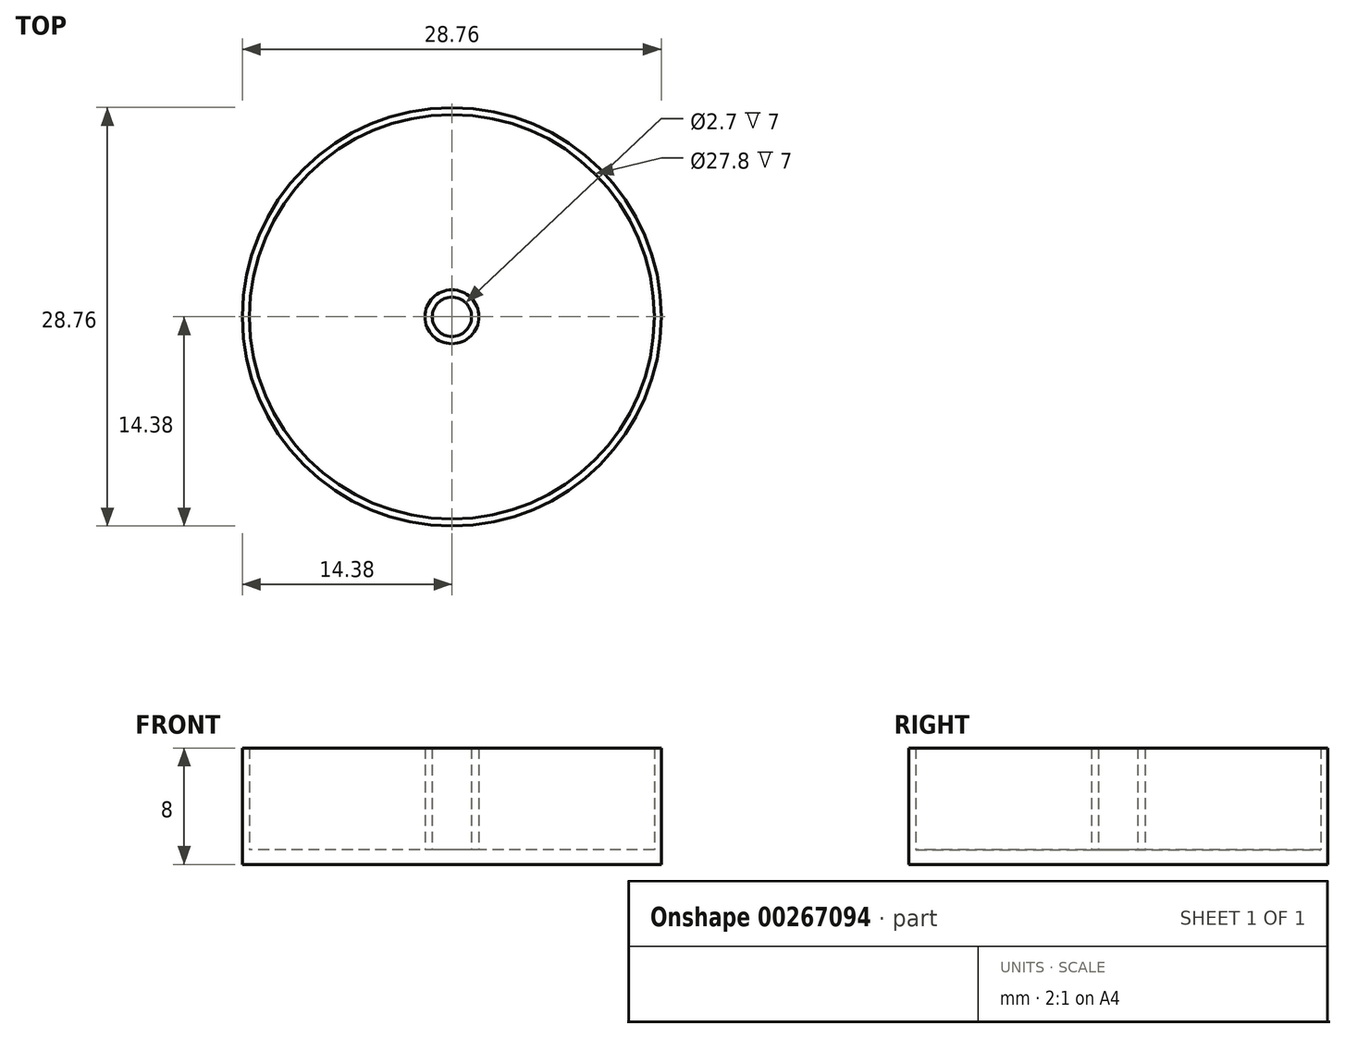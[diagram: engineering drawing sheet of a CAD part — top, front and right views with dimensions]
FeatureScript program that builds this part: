
annotation { "Feature Type Name" : "Feature", "Feature Type Description" : "" }
export const myFeature = defineFeature(function(context is Context, id is Id, definition is map)
    precondition{}
    {
        {
            var Q0;
            Q0=qCreatedBy(makeId("Top.planeOp"),FACE);
            var sketch = newSketch(context, id + "F0", { "sketchPlane" : qUnion([Q0])});
            skCircle(sketch, "E0", {"center": v(0, 0) * mm, "radius": 14.38 * mm});
            skCircle(sketch, "E1", {"center": v(0, 0) * mm, "radius": 13.9 * mm});
            skCircle(sketch, "E2", {"center": v(0, 0) * mm, "radius": 1.35 * mm});
            skCircle(sketch, "E3", {"center": v(0, 0) * mm, "radius": 1.85 * mm});
            skSolve(sketch);
        }
        {
            var Q0;
            Q0=makeQuery(id+"F0.imprint","IMPRINT",FACE,{"disambiguationData":[TD([[makeQuery(id+"F0.imprint","IMPRINT",EDGE,{"derivedFrom":sQuery(id+"F0.wireOp",EDGE,"E0")}),1.0]])]});
            var Q1;
            Q1=makeQuery(id+"F0.imprint","IMPRINT",FACE,{"disambiguationData":[TD([[makeQuery(id+"F0.imprint","IMPRINT",EDGE,{"derivedFrom":sQuery(id+"F0.wireOp",EDGE,"E1")}),1.0]])]});
            var Q2;
            Q2=makeQuery(id+"F0.imprint","IMPRINT",FACE,{"disambiguationData":[TD([[makeQuery(id+"F0.imprint","IMPRINT",EDGE,{"derivedFrom":sQuery(id+"F0.wireOp",EDGE,"E2")}),1.0]])]});
            extrude(context, id + "F1", {"entities" : qUnion([Q0, Q1, Q2]), "depth" : 1 * mm});
        }
        {
            var Q0;
            Q0=makeQuery(id+"F0.imprint","IMPRINT",FACE,{"disambiguationData":[TD([[makeQuery(id+"F0.imprint","IMPRINT",EDGE,{"derivedFrom":sQuery(id+"F0.wireOp",EDGE,"E0")}),1.0]])]});
            var Q1;
            Q1=makeQuery(id+"F0.imprint","IMPRINT",FACE,{"disambiguationData":[TD([[makeQuery(id+"F0.imprint","IMPRINT",EDGE,{"derivedFrom":sQuery(id+"F0.wireOp",EDGE,"E2")}),-1.0]])]});
            extrude(context, id + "F2", {"entities" : qUnion([Q0, Q1]), "operationType" : NewBodyOperationType.ADD, "depth" : 8 * mm});
        }
    });
